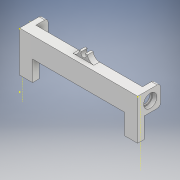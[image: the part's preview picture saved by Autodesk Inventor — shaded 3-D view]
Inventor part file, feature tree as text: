
AUTODESK INVENTOR PART (.ipt)
format: ipt  version: 2018 (Build 220112000, 112)  size: 1,077,248 bytes
history: native  units: mm
features: sketch x60, extrude x49, fillet x5
ambient origin geometry x8: Origin, YZ Plane, XZ Plane, XY Plane, X Axis, Y Axis, Z Axis, Center Point
bodies: Solid1 (feature_tree)
feature tree (114):
  extrude  "Extrusion1"  Depth=80.0mm
  extrude  "Extrusion2"  Depth=3.0mm
  sketch  "Sketch3"  dims[d5=12.0mm d6=14.5mm]
  extrude  "Extrusion3"  Depth=14.5mm
  extrude  "Extrusion4"  Depth=2.0mm
  extrude  "Extrusion5"  Depth=0.5mm TaperAngle=0.0deg
  sketch  "Sketch7"  dims[d15=10.0mm d16=25.0mm]
  extrude  "Extrusion6"  Depth=25.0mm
  extrude  "Extrusion7"  Depth=25.0mm
  extrude  "Extrusion8"  Depth=10.0mm
  fillet  "Fillet1"  Radius=10.0mm
  fillet  "Fillet2"  Radius=10.0mm
  extrude  "Extrusion9"  Depth=2.5mm TaperAngle=0.0deg
  extrude  "Extrusion10"  Depth=4.0mm
  fillet  "Fillet3"  Radius=3.0mm
  extrude  "Extrusion11"  Depth=21.0mm
  extrude  "Extrusion12"  Depth=41.0mm
  extrude  "Extrusion13"  Depth=42.0mm
  extrude  "Extrusion14"  Depth=38.0mm
  extrude  "Extrusion15"  Depth=45.0mm TaperAngle=0.0deg
  extrude  "Extrusion16"  Depth=3.0mm TaperAngle=0.0deg
  extrude  "Extrusion17"  Depth=3.0mm
  extrude  "Extrusion18"  Depth=39.5mm
  extrude  "Extrusion19"  Depth=7.25mm
  extrude  "Extrusion20"  Depth=7.75mm
  extrude  "Extrusion21"  Depth=10.0mm
  sketch  "Sketch24"  dims[d65=66.0mm d66=3.5mm d67=0.0mm]
  extrude  "Extrusion22"  Depth=10.0mm TaperAngle=0.0deg
  extrude  "Extrusion23"  Depth=16.0mm
  extrude  "Extrusion24"  Depth=3.5mm TaperAngle=0.0deg
  extrude  "Extrusion25"  Depth=2.0mm
  extrude  "Extrusion26"  Depth=2.0mm TaperAngle=0.0deg
  sketch  "Sketch30"  dims[d81=4.0mm d82=4.0mm]
  extrude  "Extrusion27"  Depth=16.0mm
  extrude  "Extrusion28"  Depth=2.0mm
  extrude  "Extrusion29"  Depth=3.5mm TaperAngle=0.0deg
  sketch  "Sketch34"  dims[d91=5.0mm d92=16.0mm d93=5.0mm]
  extrude  "Extrusion30"  Depth=4.0mm
  extrude  "Extrusion31"  Depth=2.0mm TaperAngle=0.0deg
  extrude  "Extrusion32"  Depth=150.0mm TaperAngle=0.0deg
  sketch  "Sketch38"  dims[d102=5.0mm d103=0.0mm d104=500.0mm d105=0.0mm]
  extrude  "Extrusion33"  Depth=16.0mm
  sketch  "Sketch40"  dims[d110=38.75mm d111=38.75mm]
  extrude  "Extrusion34"  Depth=16.0mm
  fillet  "Fillet4"  Radius=5.0mm
  extrude  "Extrusion35"  Depth=3.0mm
  extrude  "Extrusion36"  Depth=43.0mm TaperAngle=0.0deg
  extrude  "Extrusion37"  Depth=38.75mm
  extrude  "Extrusion38"  Depth=5.0mm TaperAngle=0.0deg
  extrude  "Extrusion39"  Depth=45.0mm TaperAngle=0.0deg
  extrude  "Extrusion40"  Depth=38.75mm
  sketch  "Sketch48"  dims[d134=16.0mm d135=5.0mm d136=0.0mm d137=7.0mm]
  extrude  "Extrusion41"  Depth=3.5mm TaperAngle=0.0deg
  extrude  "Extrusion42"  Depth=100.0mm TaperAngle=0.0deg
  extrude  "Extrusion43"  Depth=1.5mm TaperAngle=0.0deg
  sketch  "Sketch52"  dims[d144=16.0mm]
  extrude  "Extrusion44"  Depth=10.0mm
  extrude  "Extrusion45"  Depth=10.0mm
  extrude  "Extrusion46"  Depth=7.0mm
  sketch  "Sketch56"  dims[d150=5.0mm d151=0.0mm]
  sketch  "Sketch57"  dims[d152=5.0mm d153=0.0mm]
  extrude  "Extrusion47"  Depth=7.75mm
  extrude  "Extrusion48"  Depth=5.0mm TaperAngle=0.0deg
  fillet  "Fillet5"  Radius=7.0mm
  extrude  "Extrusion49"  Depth=15.0mm TaperAngle=0.0deg
  sketch  "Sketch1"  dims[d0=145.0mm d1=80.0mm]
  sketch  "Sketch2"  dims[d2=3.0mm d3=0.0mm d4=12.0mm]
  sketch  "Sketch4"  dims[d7=2.0mm d8=2.0mm]
  sketch  "Sketch5"  dims[d9=6.0mm d10=0.0mm d11=0.5mm d12=0.0mm]
  sketch  "Sketch6"  dims[d13=10.0mm d14=25.0mm]
  sketch  "Sketch8"  dims[d17=25.0mm d18=0.0mm d19=22.5mm d20=10.0mm d21=0.0mm d22=10.0mm]
  sketch  "Sketch9"  dims[d23=2.5mm d24=0.0mm d25=7.5mm d26=0.0mm]
  sketch  "Sketch10"  dims[d27=10.0mm d28=0.0mm d29=4.0mm d30=3.0mm]
  sketch  "Sketch11"  dims[d31=1.0mm d32=21.0mm]
  sketch  "Sketch12"  dims[d33=38.0mm d34=41.0mm]
  sketch  "Sketch13"  dims[d35=38.0mm d36=42.0mm]
  sketch  "Sketch14"  dims[d37=41.0mm d38=38.0mm]
  sketch  "Sketch15"  dims[d39=42.0mm d40=45.0mm d41=0.0mm]
  sketch  "Sketch16"  dims[d42=12.5mm d43=3.0mm d44=0.0mm]
  sketch  "Sketch17"  dims[d45=3.0mm d46=39.5mm]
  sketch  "Sketch18"  dims[d47=39.5mm d48=39.5mm]
  sketch  "Sketch19"  dims[d49=45.0mm d50=0.0mm d51=7.25mm]
  sketch  "Sketch20"  dims[d52=4.0mm d53=7.75mm d54=0.0mm d55=0.0mm d56=125.0mm]
  sketch  "Sketch21"  dims[d57=10.0mm d58=0.0mm d59=1.0mm]
  sketch  "Sketch22"  dims[d60=14.5mm d61=10.0mm d62=0.0mm]
  sketch  "Sketch23"  dims[d63=16.0mm d64=12.0mm]
  sketch  "Sketch25"  dims[d68=4.0mm d69=2.0mm]
  sketch  "Sketch26"  dims[d70=4.0mm d71=2.0mm d72=0.0mm]
  sketch  "Sketch27"  dims[d73=2.0mm d74=0.0mm d75=16.0mm]
  sketch  "Sketch28"  dims[d76=2.0mm d77=2.0mm]
  sketch  "Sketch29"  dims[d78=2.0mm d79=3.5mm d80=0.0mm]
  sketch  "Sketch31"  dims[d83=4.0mm d84=2.0mm d85=0.0mm]
  sketch  "Sketch32"  dims[d86=15.5mm d87=150.0mm d88=0.0mm]
  sketch  "Sketch33"  dims[d89=12.0mm d90=16.0mm]
  sketch  "Sketch35"  dims[d94=12.0mm d95=3.0mm]
  sketch  "Sketch36"  dims[d96=43.0mm d97=0.0mm d98=43.0mm d99=0.0mm]
  sketch  "Sketch37"  dims[d100=38.75mm d101=38.75mm]
  sketch  "Sketch39"  dims[d106=45.0mm d107=0.0mm d108=45.0mm d109=0.0mm]
  sketch  "Sketch41"  dims[d112=45.0mm d113=0.0mm d114=3.5mm d115=0.0mm]
  sketch  "Sketch42"  dims[d116=43.0mm d117=0.0mm d118=100.0mm d119=0.0mm]
  sketch  "Sketch43"  dims[d120=200.0mm d121=0.0mm d122=1.5mm d123=0.0mm]
  sketch  "Sketch44"  dims[d124=5.0mm d125=10.0mm]
  sketch  "Sketch45"  dims[d126=10.0mm d127=6.35mm]
  sketch  "Sketch46"  dims[d128=7.0mm d129=0.0mm d130=2.75mm]
  sketch  "Sketch47"  dims[d131=7.0mm d132=0.0mm d133=7.75mm]
  sketch  "Sketch49"  dims[d138=7.0mm d139=15.0mm d140=0.0mm]
  sketch  "Sketch50"  dims[d141=13.5mm]
  sketch  "Sketch51"  dims[d142=2.0mm d143=0.0mm]
  sketch  "Sketch53"  dims[d145=5.0mm d146=0.0mm]
  sketch  "Sketch54"  dims[d147=2.0mm d148=0.0mm]
  sketch  "Sketch55"  dims[d149=16.25mm]
  sketch  "Sketch58"  dims[d154=3.0mm d155=0.0mm]
  sketch  "Sketch59"  dims[d156=3.0mm d157=0.0mm]
  sketch  "Sketch60"  dims[d158=12.25mm d159=3.5mm d160=43.0mm d161=0.0mm d162=12.25mm d163=3.5mm d164=43.0mm d165=0.0mm d166=18.0mm d167=43.0mm d168=0.0mm d169=131.0mm d170=0.0mm d171=131.0mm d172=0.0mm d173=0.5mm d174=2.0mm d175=0.0mm]
